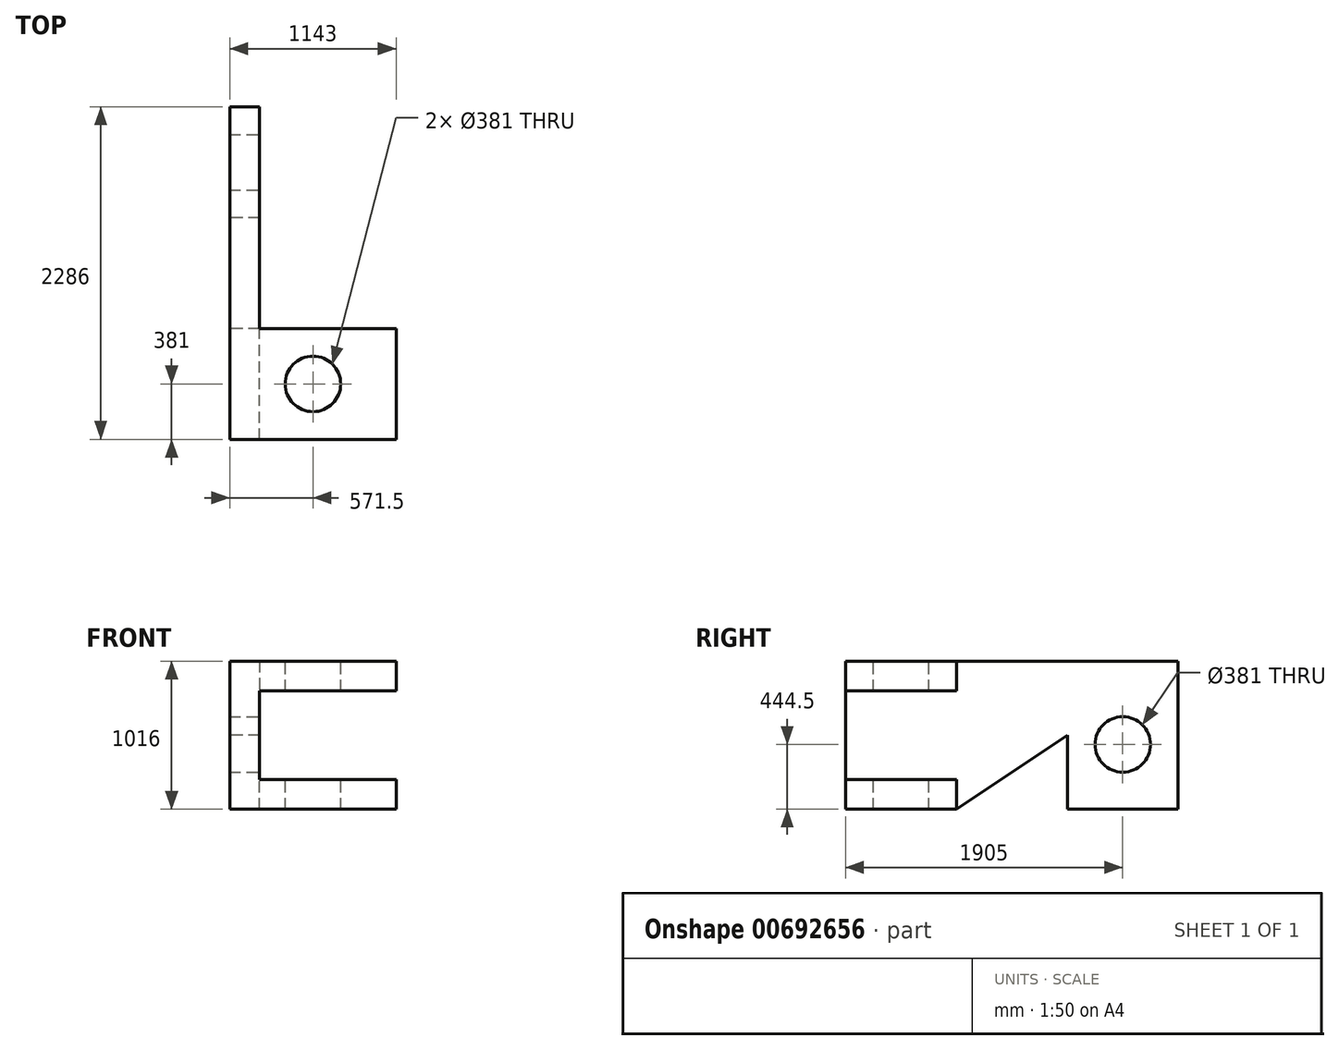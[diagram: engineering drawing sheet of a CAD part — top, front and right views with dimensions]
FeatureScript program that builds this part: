
annotation { "Feature Type Name" : "Feature", "Feature Type Description" : "" }
export const myFeature = defineFeature(function(context is Context, id is Id, definition is map)
    precondition{}
    {
        {
            var Q0;
            Q0=qCreatedBy(makeId("Right.planeOp"),FACE);
            var sketch = newSketch(context, id + "F0", { "sketchPlane" : qUnion([Q0])});
            skLineSegment(sketch, "E0.bottom", {"start": v(0, 0) * mm, "end": v(762, 0) * mm});
            skLineSegment(sketch, "E0.top", {"start": v(0, 1016) * mm, "end": v(2286, 1016) * mm});
            skLineSegment(sketch, "E0.left", {"start": v(0, 0) * mm, "end": v(0, 1016) * mm});
            skLineSegment(sketch, "E0.right", {"start": v(2286, 0) * mm, "end": v(2286, 1016) * mm});
            skPoint(sketch, "E1", {"position": v(1524, 0) * mm});
            skLineSegment(sketch, "E2", {"start": v(1524, 0) * mm, "end": v(1524, 508) * mm});
            skPoint(sketch, "E3", {"position": v(762, 0) * mm});
            skLineSegment(sketch, "E4", {"start": v(762, 0) * mm, "end": v(1524, 508) * mm});
            skLineSegment(sketch, "E5.trimOffspring", {"start": v(1524, 0) * mm, "end": v(2286, 0) * mm});
            skSolve(sketch);
        }
        {
            var Q0;
            Q0=makeQuery(id+"F0.imprint","IMPRINT",FACE,{"disambiguationData":[TD([[makeQuery(id+"F0.imprint","IMPRINT",EDGE,{"derivedFrom":sQuery(id+"F0.wireOp",EDGE,"E0.bottom")}),1.0]])]});
            var Q1;
            Q1 = qSketchRegion(id + "F0", true);
            extrude(context, id + "F1", {"entities" : qUnion([Q0, Q1]), "depth" : 203.2 * mm, "offsetDistance" : 25.4 * mm});
        }
        {
            var Q0;
            Q0=makeQuery(id+"F1.opExtrude","CAP_FACE",FACE,{"disambiguationData":[OSD([sQuery(id+"F0.wireOp",EDGE,"E0.bottom"),sQuery(id+"F0.wireOp",EDGE,"E0.top"),sQuery(id+"F0.wireOp",EDGE,"E0.left"),sQuery(id+"F0.wireOp",EDGE,"E0.right"),sQuery(id+"F0.wireOp",EDGE,"E2"),sQuery(id+"F0.wireOp",EDGE,"E4"),sQuery(id+"F0.wireOp",EDGE,"E5.trimOffspring")])],"isStart":false});
            var sketch = newSketch(context, id + "F2", { "sketchPlane" : qUnion([Q0])});
            skLineSegment(sketch, "E6.bottom", {"start": v(762, 0) * mm, "end": v(0, 0) * mm});
            skLineSegment(sketch, "E6.top", {"start": v(762, 203.2) * mm, "end": v(0, 203.2) * mm});
            skLineSegment(sketch, "E6.left", {"start": v(762, 0) * mm, "end": v(762, 203.2) * mm});
            skLineSegment(sketch, "E6.right", {"start": v(0, 0) * mm, "end": v(0, 203.2) * mm});
            skLineSegment(sketch, "E7.bottom", {"start": v(0, 1016) * mm, "end": v(762, 1016) * mm});
            skLineSegment(sketch, "E7.top", {"start": v(0, 812.8) * mm, "end": v(762, 812.8) * mm});
            skLineSegment(sketch, "E7.left", {"start": v(0, 1016) * mm, "end": v(0, 812.8) * mm});
            skLineSegment(sketch, "E7.right", {"start": v(762, 1016) * mm, "end": v(762, 812.8) * mm});
            skSolve(sketch);
        }
        {
            var Q0;
            Q0 = qSketchRegion(id + "F2", true);
            extrude(context, id + "F3", {"entities" : qUnion([Q0]), "operationType" : NewBodyOperationType.ADD, "depth" : 939.8 * mm, "offsetDistance" : 25.4 * mm});
        }
        {
            var Q0;
            Q0=makeQuery(id+"F3.boolean.opBoolean","MERGE",FACE,{"derivedFrom":[makeQuery(id+"F1.opExtrude","SWEPT_FACE",FACE,{"disambiguationData":[OSD([sQuery(id+"F0.wireOp",EDGE,"E0.top")])]}),makeQuery(id+"F3.opExtrude","SWEPT_FACE",FACE,{"disambiguationData":[OSD([sQuery(id+"F2.wireOp",EDGE,"E7.bottom")])]})]});
            var sketch = newSketch(context, id + "F4", { "sketchPlane" : qUnion([Q0])});
            skPoint(sketch, "E8", {"position": v(1143, 381) * mm});
            skPoint(sketch, "E9.endSnap0", {"position": v(673.1, 762) * mm});
            skCircle(sketch, "E10", {"center": v(571.5, 381) * mm, "radius": 190.5 * mm});
            skPoint(sketch, "E11", {"position": v(762, 381) * mm});
            skSolve(sketch);
        }
        {
            var Q0;
            Q0=sQuery(id+"F4.wireOp",VERTEX,"E10.center");
            var Q1;
            Q1=makeQuery(id+"F1.opExtrude","SWEPT_BODY",BODY,{"disambiguationData":[OSD([sQuery(id+"F0.wireOp",EDGE,"E0.bottom"),sQuery(id+"F0.wireOp",EDGE,"E0.top"),sQuery(id+"F0.wireOp",EDGE,"E0.left"),sQuery(id+"F0.wireOp",EDGE,"E0.right"),sQuery(id+"F0.wireOp",EDGE,"E2"),sQuery(id+"F0.wireOp",EDGE,"E4"),sQuery(id+"F0.wireOp",EDGE,"E5.trimOffspring")])]});
            hole(context, id + "F5", {"style" : HoleStyle.SIMPLE, "endStyle" : HoleEndStyle.THROUGH, "holeDiameter" : 381 * mm, "majorDiameter" : 6.35 * mm, "isTappedThrough" : true, "tappedDepth" : 12.7 * mm, "tapClearance" : 3, "locations" : qUnion([Q0]), "scope" : qUnion([Q1])});
        }
        {
            var Q0;
            Q0=makeQuery(id+"F1.opExtrude","CAP_FACE",FACE,{"disambiguationData":[OSD([sQuery(id+"F0.wireOp",EDGE,"E0.bottom"),sQuery(id+"F0.wireOp",EDGE,"E0.top"),sQuery(id+"F0.wireOp",EDGE,"E0.left"),sQuery(id+"F0.wireOp",EDGE,"E0.right"),sQuery(id+"F0.wireOp",EDGE,"E2"),sQuery(id+"F0.wireOp",EDGE,"E4"),sQuery(id+"F0.wireOp",EDGE,"E5.trimOffspring")])],"isStart":false});
            var sketch = newSketch(context, id + "F6", { "sketchPlane" : qUnion([Q0])});
            skLineSegment(sketch, "E12", {"start": v(1905, 0) * mm, "end": v(1905, 1016) * mm});
            skLineSegment(sketch, "E13", {"start": v(1905, 1016) * mm, "end": v(1905, 444.5) * mm});
            skPoint(sketch, "E14", {"position": v(1905, 444.5) * mm});
            skCircle(sketch, "E15", {"center": v(1905, 444.5) * mm, "radius": 250.6 * mm});
            skSolve(sketch);
        }
        {
            var Q0;
            Q0=sQuery(id+"F6.wireOp",VERTEX,"E14");
            var Q1;
            Q1=makeQuery(id+"F1.opExtrude","SWEPT_BODY",BODY,{"disambiguationData":[OSD([sQuery(id+"F0.wireOp",EDGE,"E0.bottom"),sQuery(id+"F0.wireOp",EDGE,"E0.top"),sQuery(id+"F0.wireOp",EDGE,"E0.left"),sQuery(id+"F0.wireOp",EDGE,"E0.right"),sQuery(id+"F0.wireOp",EDGE,"E2"),sQuery(id+"F0.wireOp",EDGE,"E4"),sQuery(id+"F0.wireOp",EDGE,"E5.trimOffspring")])]});
            hole(context, id + "F7", {"style" : HoleStyle.SIMPLE, "endStyle" : HoleEndStyle.THROUGH, "holeDiameter" : 381 * mm, "majorDiameter" : 6.35 * mm, "isTappedThrough" : true, "tappedDepth" : 12.7 * mm, "tapClearance" : 3, "locations" : qUnion([Q0]), "scope" : qUnion([Q1])});
        }
    });
